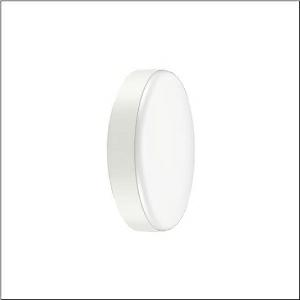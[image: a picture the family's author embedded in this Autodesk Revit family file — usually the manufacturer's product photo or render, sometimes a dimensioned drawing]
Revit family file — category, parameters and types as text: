
# Revit family: round_31_51wc10db44a
name_source: partatom
category: Lighting Fixtures
units: mm (PartAtom-declared; Revit-internal decimal feet)

## family parameters
Cut with Voids When Loaded = No
Host = Face
Light Source = No
Part Type = Normal
Room Calculation Point = No
Round Connector Dimension = Use Diameter
Shared = No

## types (1)
- Round 31 (1 x LED, 4400 lm, 34 W, 4000K)
    Apparent Load = 34 VA
    CIE Flux Codes = 44 75 94 94 100
    Color Rendering = 80
    Color Temperature = 4000K
    Default Elevation = 1800 mm
    Description = Round 31, wall and ceiling luminaire, primary optical cover: cover, of PC, opal, light emission: direct distribution, primary light characteristic: symmetric, installation type: surface-mounted, LED, rated luminous flux: 4.400lm, luminous efficacy: 129lm/W, light colour: 840, colour temperature: 4000K, control gear: DALI 2, with terminal, 3-pole, max. 2.5mm², mains connection: 220..240V, AC, 50/60Hz, rated input power: 34W, luminaire housing, of PC, traffic white (RAL 9016), diameter: 480mm, protection rating (complete): IP65, insulation class (complete): insulation class II (safety insulation), certification: CE, impact resistance: IK10, permissible operating ambient temperature: -20..+40°C, permissible storage temperature: -20..+60°C, packaging unit: 1 piece
    Height = 97 mm
    Lamp = 1 x LED
    Lamp Light Flux = 4400 lm
    Lamp Power = 34 W
    Lamp count = 1
    Length = 480 mm
    Luminous efficacy = 129 lm/W
    Manufacturer = Siteco
    ModVariant = No
    Model = 51WC10DB44A
    Mounting Place = Ceiling
    Mounting Type = Surface mounted
    Number of Poles = 1
    OnlyDefault = Yes
    Power Factor = 1
    Product Name = Round 31
    Product group = wall and ceiling luminaire
    ProductGroupID = 304
    Protection Class = Protection class II
    Protection Degree = IP 65
    RLX_Detail_Level = 1
    RLX_Emergency_Light_Flux = 0 lm
    RLX_Emergency_Type = 0
    RLX_Emergency_Type_DB = No
    RlxData = <blob elided: 55329 chars, md5=8b0bdbbd>
    Socket = socket
    Standby Power = 0 W
    System Light Flux = 4400 lm
    System Power = 34 W
    Type Comments = Product without accessories
    Type Image = l_1007188.jpg
    URL = http://relux.com
    VarID = ---
    Voltage = 0 V
    Weight = 0.00 kg
    Width = 0 mm  [stored 0 ft]

note: [stored X ft] marks values corroborated as IEEE doubles in the binary element streams (Revit-internal decimal feet)

## geometry (parser evidence)
native form markers: Blend x4, Sweep x13
no freeform markers — native parametric forms only
